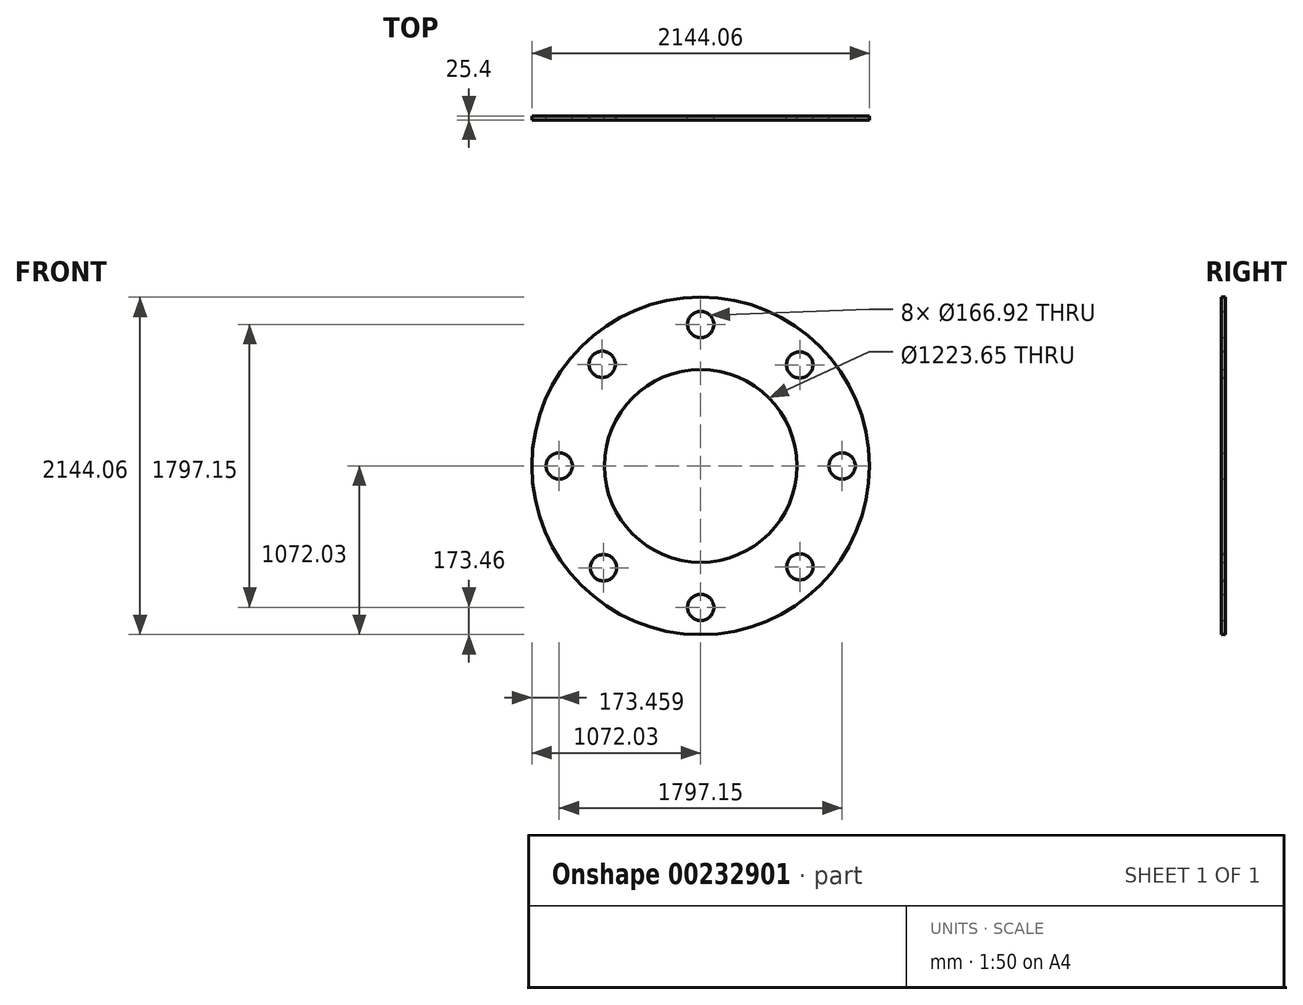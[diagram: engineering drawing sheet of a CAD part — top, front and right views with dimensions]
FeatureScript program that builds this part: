
annotation { "Feature Type Name" : "Feature", "Feature Type Description" : "" }
export const myFeature = defineFeature(function(context is Context, id is Id, definition is map)
    precondition{}
    {
        {
            var Q0;
            Q0=qCreatedBy(makeId("Front.planeOp"),FACE);
            var sketch = newSketch(context, id + "F0", { "sketchPlane" : qUnion([Q0])});
            skCircle(sketch, "E0", {"center": v(-942.92, 928.72) * mm, "radius": 1072.03 * mm});
            skCircle(sketch, "E1", {"center": v(-942.92, 928.72) * mm, "radius": 898.57 * mm});
            skCircle(sketch, "E2", {"center": v(-942.92, 928.72) * mm, "radius": 611.82 * mm});
            skCircle(sketch, "E3", {"center": v(-942.92, 1827.3) * mm, "radius": 83.46 * mm});
            skCircle(sketch, "E4", {"center": v(-942.92, 30.15) * mm, "radius": 83.46 * mm});
            skCircle(sketch, "E5", {"center": v(-1841.5, 928.72) * mm, "radius": 83.46 * mm});
            skCircle(sketch, "E6", {"center": v(-44.34, 928.72) * mm, "radius": 83.46 * mm});
            skCircle(sketch, "E7", {"center": v(-1568.34, 1573.93) * mm, "radius": 83.46 * mm});
            skCircle(sketch, "E8", {"center": v(-313.03, 287.88) * mm, "radius": 83.46 * mm});
            skCircle(sketch, "E9", {"center": v(-1560.09, 282.07) * mm, "radius": 83.46 * mm});
            skCircle(sketch, "E10", {"center": v(-313.71, 1570.4) * mm, "radius": 83.46 * mm});
            skSolve(sketch);
        }
        {
            var Q0;
            Q0=makeQuery(id+"F0.imprint","IMPRINT",FACE,{"disambiguationData":[TD([[makeQuery(id+"F0.imprint","IMPRINT",EDGE,{"derivedFrom":sQuery(id+"F0.wireOp",EDGE,"E0")}),1.0]])]});
            var Q1;
            Q1=makeQuery(id+"F0.imprint","IMPRINT",FACE,{"disambiguationData":[TD([[makeQuery(id+"F0.imprint","IMPRINT",EDGE,{"derivedFrom":sQuery(id+"F0.wireOp",EDGE,"E2")}),-1.0]])]});
            extrude(context, id + "F1", {"entities" : qUnion([Q0, Q1]), "depth" : 25.4 * mm});
        }
    });
